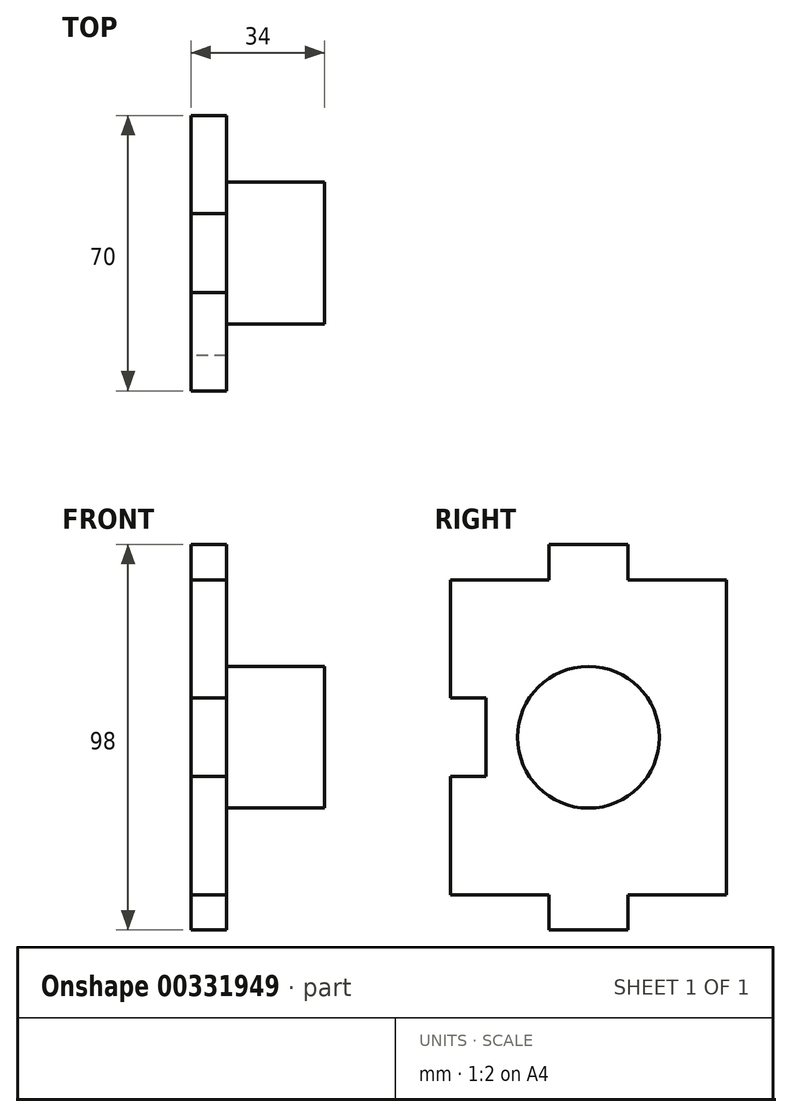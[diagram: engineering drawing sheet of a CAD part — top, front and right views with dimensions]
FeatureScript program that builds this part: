
annotation { "Feature Type Name" : "Feature", "Feature Type Description" : "" }
export const myFeature = defineFeature(function(context is Context, id is Id, definition is map)
    precondition{}
    {
        {
            var Q0;
            Q0=qCreatedBy(makeId("Right.planeOp"),FACE);
            var sketch = newSketch(context, id + "F0", { "sketchPlane" : qUnion([Q0])});
            skLineSegment(sketch, "E0.bottom", {"start": v(10, 49) * mm, "end": v(-10, 49) * mm});
            skLineSegment(sketch, "E0.top", {"start": v(10, -49) * mm, "end": v(-10, -49) * mm});
            skLineSegment(sketch, "E0.left", {"start": v(35, 40) * mm, "end": v(35, -40) * mm});
            skLineSegment(sketch, "E0.right", {"start": v(-35, 40) * mm, "end": v(-35, 10) * mm});
            skPoint(sketch, "E0.middle", {"position": v(0, 0) * mm});
            skLineSegment(sketch, "E1", {"start": v(-35, 40) * mm, "end": v(-10, 40) * mm});
            skLineSegment(sketch, "E2", {"start": v(-35, -40) * mm, "end": v(-10, -40) * mm});
            skLineSegment(sketch, "E3", {"start": v(-26, 10) * mm, "end": v(-26, -10) * mm});
            skLineSegment(sketch, "E4", {"start": v(10, 49) * mm, "end": v(10, 40) * mm});
            skLineSegment(sketch, "E5", {"start": v(-10, 40) * mm, "end": v(-10, 49) * mm});
            skLineSegment(sketch, "E6", {"start": v(-10, -40) * mm, "end": v(-10, -49) * mm});
            skLineSegment(sketch, "E7", {"start": v(10, -40) * mm, "end": v(10, -49) * mm});
            skPoint(sketch, "E8.orphan", {"position": v(-35, 49) * mm});
            skPoint(sketch, "E9.orphan", {"position": v(35, 49) * mm});
            skPoint(sketch, "E10.orphan", {"position": v(35, -49) * mm});
            skPoint(sketch, "E11.trimOffspring.start.orphan", {"position": v(-26, -49) * mm});
            skPoint(sketch, "E12.orphan", {"position": v(-35, -49) * mm});
            skLineSegment(sketch, "E13", {"start": v(10, 40) * mm, "end": v(37.46, 40) * mm});
            skLineSegment(sketch, "E14.trimOffspring", {"start": v(10, -40) * mm, "end": v(35, -40) * mm});
            skLineSegment(sketch, "E15", {"start": v(-35, 10) * mm, "end": v(-26, 10) * mm});
            skLineSegment(sketch, "E16", {"start": v(-35, -10) * mm, "end": v(-26, -10) * mm});
            skLineSegment(sketch, "E17.trimOffspring", {"start": v(-35, -10) * mm, "end": v(-35, -40) * mm});
            skSolve(sketch);
        }
        {
            var Q0;
            Q0 = qSketchRegion(id + "F0", true);
            extrude(context, id + "F1", {"entities" : qUnion([Q0]), "depth" : 9 * mm});
        }
        {
            var Q0;
            Q0=makeQuery(id+"F1.opExtrude","CAP_FACE",FACE,{"disambiguationData":[OSD([sQuery(id+"F0.wireOp",EDGE,"E0.bottom"),sQuery(id+"F0.wireOp",EDGE,"E0.top"),sQuery(id+"F0.wireOp",EDGE,"E0.left"),sQuery(id+"F0.wireOp",EDGE,"E0.right"),sQuery(id+"F0.wireOp",EDGE,"E1"),sQuery(id+"F0.wireOp",EDGE,"E2"),sQuery(id+"F0.wireOp",EDGE,"E3"),sQuery(id+"F0.wireOp",EDGE,"E4"),sQuery(id+"F0.wireOp",EDGE,"E5"),sQuery(id+"F0.wireOp",EDGE,"E6"),sQuery(id+"F0.wireOp",EDGE,"E7"),sQuery(id+"F0.wireOp",EDGE,"E13"),sQuery(id+"F0.wireOp",EDGE,"E14.trimOffspring"),sQuery(id+"F0.wireOp",EDGE,"E15"),sQuery(id+"F0.wireOp",EDGE,"E16"),sQuery(id+"F0.wireOp",EDGE,"E17.trimOffspring")])],"isStart":false});
            var sketch = newSketch(context, id + "F2", { "sketchPlane" : qUnion([Q0])});
            skCircle(sketch, "E18", {"center": v(0, 0) * mm, "radius": 18.01 * mm});
            skSolve(sketch);
        }
        {
            var Q0;
            Q0=makeQuery(id+"F2.imprint","IMPRINT",FACE,{"disambiguationData":[TD([[makeQuery(id+"F2.imprint","IMPRINT",EDGE,{"derivedFrom":sQuery(id+"F2.wireOp",EDGE,"E18")}),1.0]])]});
            extrude(context, id + "F3", {"entities" : qUnion([Q0]), "operationType" : NewBodyOperationType.ADD, "depth" : 25 * mm});
        }
    });
